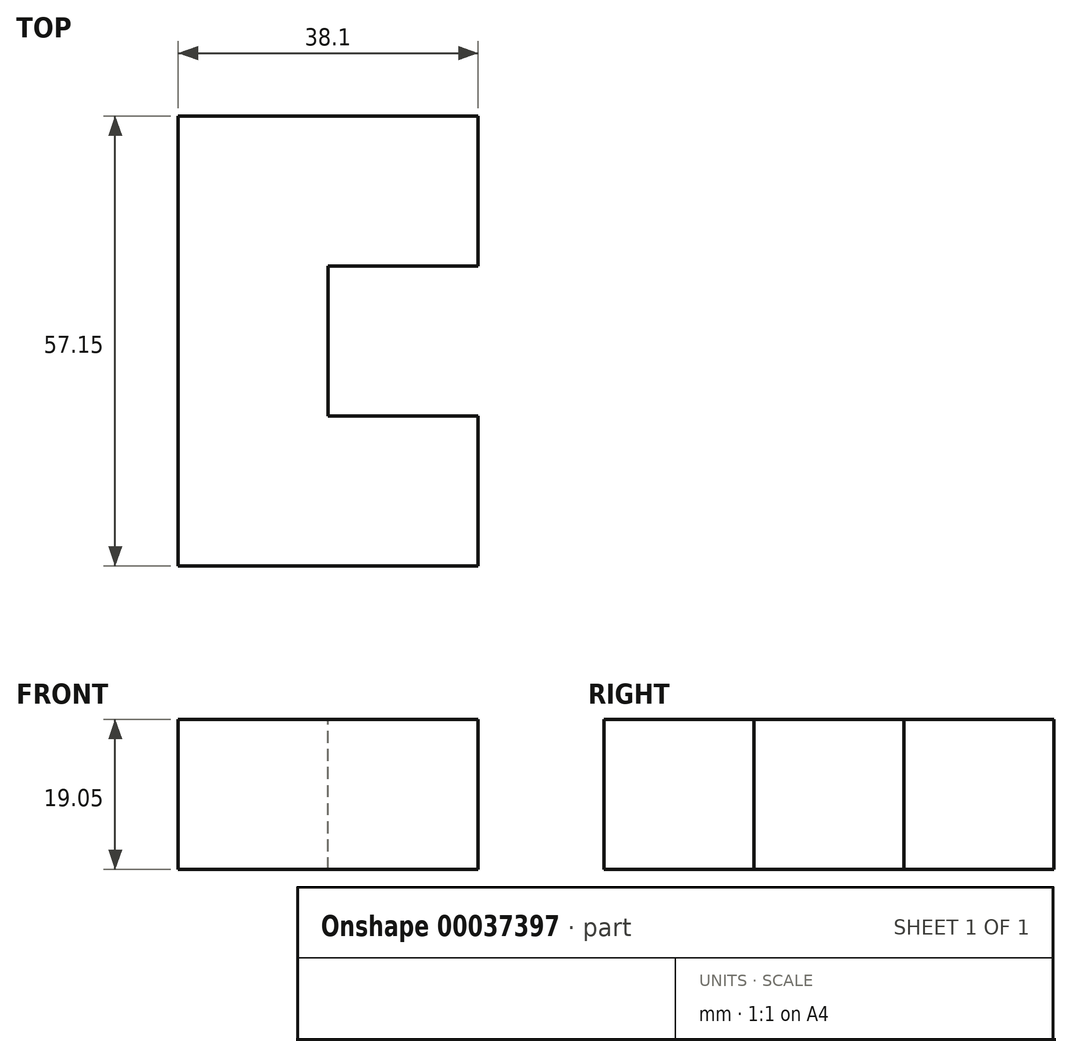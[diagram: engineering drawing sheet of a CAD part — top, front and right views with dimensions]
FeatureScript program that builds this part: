
annotation { "Feature Type Name" : "Feature", "Feature Type Description" : "" }
export const myFeature = defineFeature(function(context is Context, id is Id, definition is map)
    precondition{}
    {
        {
            var Q0;
            Q0=qCreatedBy(makeId("Top.planeOp"),FACE);
            var sketch = newSketch(context, id + "F0", { "sketchPlane" : qUnion([Q0])});
            skLineSegment(sketch, "E0.bottom", {"start": v(0, 0) * mm, "end": v(38.1, 0) * mm});
            skLineSegment(sketch, "E0.top", {"start": v(0, 57.15) * mm, "end": v(38.1, 57.15) * mm});
            skLineSegment(sketch, "E0.left", {"start": v(0, 0) * mm, "end": v(0, 57.15) * mm});
            skLineSegment(sketch, "E0.right", {"start": v(38.1, 0) * mm, "end": v(38.1, 57.15) * mm});
            skSolve(sketch);
        }
        {
            var Q0;
            Q0 = qSketchRegion(id + "F0", true);
            extrude(context, id + "F1", {"entities" : qUnion([Q0]), "depth" : 19.05 * mm});
        }
        {
            var Q0;
            Q0=makeQuery(id+"F1.opExtrude","SWEPT_FACE",FACE,{"disambiguationData":[OSD([sQuery(id+"F0.wireOp",EDGE,"E0.right")])]});
            var sketch = newSketch(context, id + "F2", { "sketchPlane" : qUnion([Q0])});
            skLineSegment(sketch, "E1.bottom", {"start": v(28.57, 0) * mm, "end": v(19.05, 0) * mm});
            skLineSegment(sketch, "E1.top", {"start": v(28.57, 19.05) * mm, "end": v(19.05, 19.05) * mm});
            skLineSegment(sketch, "E1.left", {"start": v(28.57, 0) * mm, "end": v(28.57, 19.05) * mm});
            skLineSegment(sketch, "E1.right", {"start": v(19.05, 0) * mm, "end": v(19.05, 19.05) * mm});
            skSolve(sketch);
        }
        {
            var Q0;
            Q0 = qSketchRegion(id + "F2", true);
            extrude(context, id + "F3", {"entities" : qUnion([Q0]), "operationType" : NewBodyOperationType.REMOVE, "oppositeDirection" : true, "depth" : 19.05 * mm});
        }
        {
            var Q0;
            {var subQ0=sQuery(id+"F0.wireOp",EDGE,"E0.right");var subQ1=sQuery(id+"F0.wireOp",EDGE,"E0.top");Q0=makeQuery(id+"F3.boolean.opBoolean","SPLIT",FACE,{"disambiguationData":[TD([makeQuery(id+"F1.opExtrude","SWEPT_FACE",FACE,{"disambiguationData":[OSD([subQ1])]})])],"derivedFrom":makeQuery(id+"F1.opExtrude","SWEPT_FACE",FACE,{"disambiguationData":[OSD([subQ0])]})});}
            var sketch = newSketch(context, id + "F4", { "sketchPlane" : qUnion([Q0])});
            skLineSegment(sketch, "E2.bottom", {"start": v(28.57, 0) * mm, "end": v(38.1, 0) * mm});
            skLineSegment(sketch, "E2.top", {"start": v(28.57, 19.05) * mm, "end": v(38.1, 19.05) * mm});
            skLineSegment(sketch, "E2.left", {"start": v(28.57, 0) * mm, "end": v(28.57, 19.05) * mm});
            skLineSegment(sketch, "E2.right", {"start": v(38.1, 0) * mm, "end": v(38.1, 19.05) * mm});
            skSolve(sketch);
        }
        {
            var Q0;
            Q0 = qSketchRegion(id + "F4", true);
            extrude(context, id + "F5", {"entities" : qUnion([Q0]), "operationType" : NewBodyOperationType.REMOVE, "oppositeDirection" : true, "depth" : 19.05 * mm});
        }
    });
